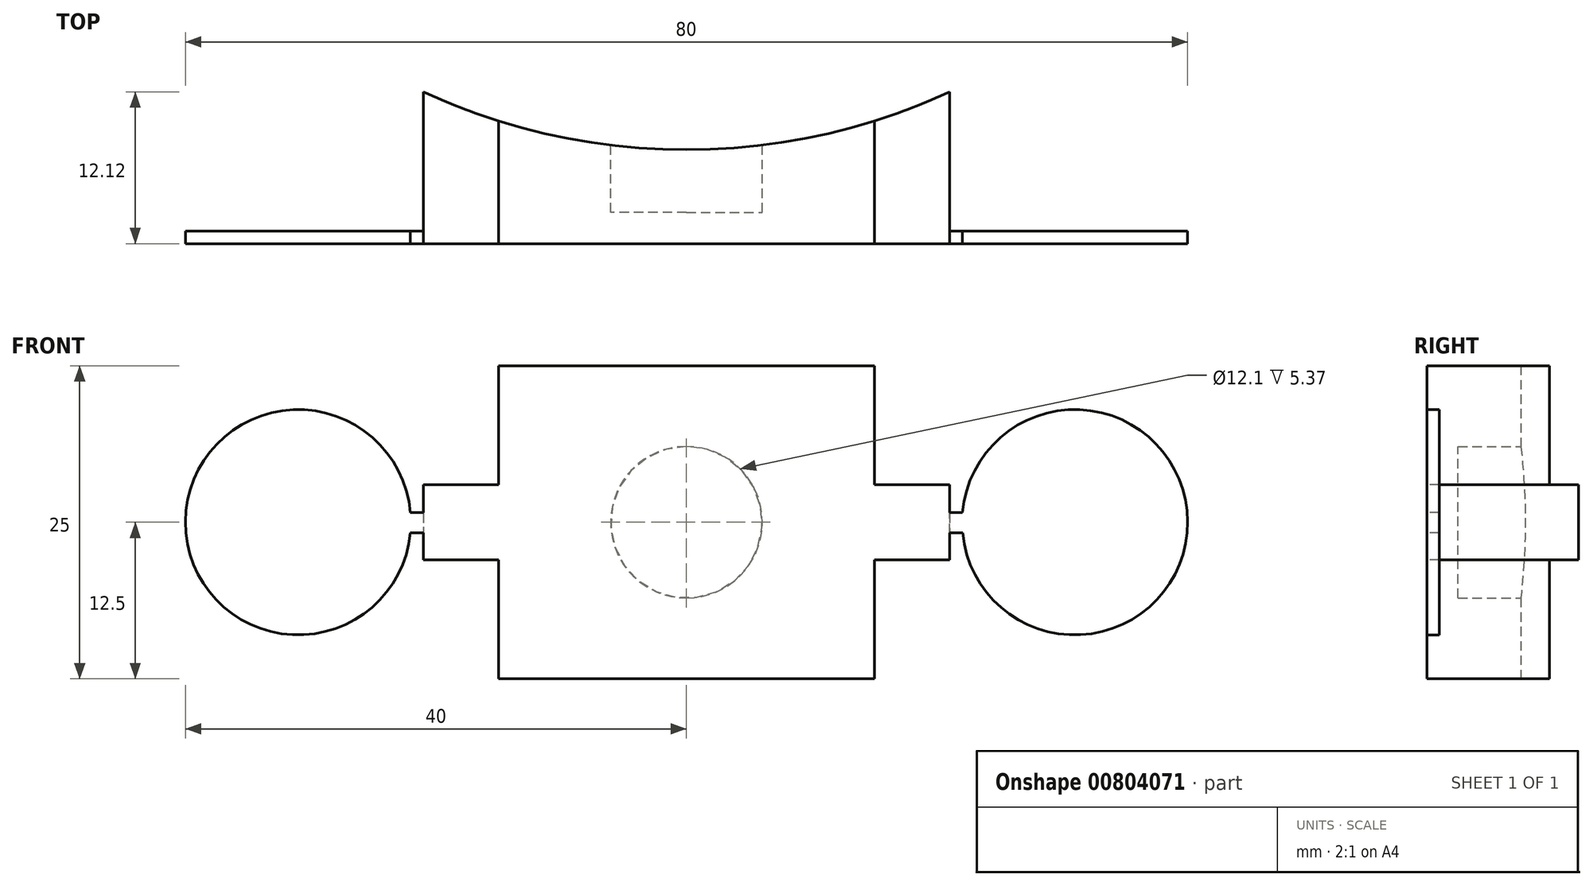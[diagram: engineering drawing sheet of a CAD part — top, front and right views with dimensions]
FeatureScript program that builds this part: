
annotation { "Feature Type Name" : "Feature", "Feature Type Description" : "" }
export const myFeature = defineFeature(function(context is Context, id is Id, definition is map)
    precondition{}
    {
        {
            var Q0;
            Q0=qCreatedBy(makeId("Top.planeOp"),FACE);
            var sketch = newSketch(context, id + "F0", { "sketchPlane" : qUnion([Q0])});
            skArc(sketch, "E0", {"start": v(-50, 0) * mm, "mid": v(0, -50) * mm, "end": v(50, 0) * mm});
            skArc(sketch, "E1", {"start": v(-55, 0) * mm, "mid": v(0, -55) * mm, "end": v(55, 0) * mm});
            skLineSegment(sketch, "E2", {"start": v(-55, 0) * mm, "end": v(-50, 0) * mm});
            skLineSegment(sketch, "E3.trimOffspring", {"start": v(50, 0) * mm, "end": v(55, 0) * mm});
            skSolve(sketch);
        }
        {
            var Q0;
            Q0=qSketchRegion(id+"F0",true);
            extrude(context, id + "F1", {"entities" : qUnion([Q0]), "endBound" : BoundingType.SYMMETRIC, "depth" : 25 * mm, "offsetDistance" : 25 * mm});
        }
        {
            var Q0;
            Q0=makeQuery(id+"F1.opExtrude","CAP_FACE",FACE,{"disambiguationData":[OSD([sQuery(id+"F0.wireOp",EDGE,"E0"),sQuery(id+"F0.wireOp",EDGE,"E1")])],"isStart":false});
            var sketch = newSketch(context, id + "F2", { "sketchPlane" : qUnion([Q0])});
            skLineSegment(sketch, "E4", {"start": v(-55, 0) * mm, "end": v(-55, -57.5) * mm});
            skLineSegment(sketch, "E5", {"start": v(55, 0) * mm, "end": v(55, -57.5) * mm});
            skLineSegment(sketch, "E6", {"start": v(0, -57.5) * mm, "end": v(55, -57.5) * mm});
            skLineSegment(sketch, "E7", {"start": v(0, -57.5) * mm, "end": v(-55, -57.5) * mm});
            skArc(sketch, "E8", {"start": v(-55, 0) * mm, "mid": v(0, -55) * mm, "end": v(55, 0) * mm});
            skLineSegment(sketch, "E9", {"start": v(0, -55) * mm, "end": v(0, -57.5) * mm, "construction": true});
            skSolve(sketch);
        }
        {
            var Q0;
            Q0=qSketchRegion(id+"F2",true);
            extrude(context, id + "F3", {"entities" : qUnion([Q0]), "operationType" : NewBodyOperationType.ADD, "oppositeDirection" : true, "depth" : 25 * mm, "offsetDistance" : 25 * mm});
        }
        {
            var Q0;
            Q0=qCreatedBy(makeId("Front.planeOp"),FACE);
            var sketch = newSketch(context, id + "F4", { "sketchPlane" : qUnion([Q0])});
            skCircle(sketch, "E10", {"center": v(0, 0) * mm, "radius": 6.05 * mm});
            skSolve(sketch);
        }
        {
            var Q0;
            Q0=qSketchRegion(id+"F4",true);
            extrude(context, id + "F5", {"entities" : qUnion([Q0]), "operationType" : NewBodyOperationType.REMOVE, "depth" : 55 * mm, "offsetDistance" : 25 * mm});
        }
        {
            var Q0;
            Q0=qCreatedBy(makeId("Right.planeOp"),FACE);
            var sketch = newSketch(context, id + "F6", { "sketchPlane" : qUnion([Q0])});
            skLineSegment(sketch, "E11", {"start": v(0, 0) * mm, "end": v(-11, 0) * mm, "construction": true});
            skCircle(sketch, "E12", {"center": v(-11, 0) * mm, "radius": 9.05 * mm});
            skSolve(sketch);
        }
        {
            var Q0;
            Q0=qSketchRegion(id+"F6",true);
            extrude(context, id + "F7", {"entities" : qUnion([Q0]), "operationType" : NewBodyOperationType.REMOVE, "endBound" : BoundingType.SYMMETRIC, "oppositeDirection" : true, "depth" : 105 * mm, "offsetDistance" : 25 * mm});
        }
        {
            var Q0;
            Q0=makeQuery(id+"F3.opExtrude","SWEPT_FACE",FACE,{"disambiguationData":[OSD([sQuery(id+"F2.wireOp",EDGE,"E6"),sQuery(id+"F2.wireOp",EDGE,"E7")])]});
            var sketch = newSketch(context, id + "F8", { "sketchPlane" : qUnion([Q0])});
            skLineSegment(sketch, "E13", {"start": v(55, 0) * mm, "end": v(65, 0) * mm, "construction": true});
            skLineSegment(sketch, "E14", {"start": v(-55, 0) * mm, "end": v(-65, 0) * mm, "construction": true});
            skArc(sketch, "E15", {"start": v(56.19, -1.83) * mm, "mid": v(74, 0.24) * mm, "end": v(56.1, 1.35) * mm});
            skArc(sketch, "E16", {"start": v(-56.02, 0.59) * mm, "mid": v(-74, -0.07) * mm, "end": v(-56.01, -0.44) * mm});
            skLineSegment(sketch, "E17", {"start": v(0, -12.5) * mm, "end": v(-55, -12.5) * mm, "construction": true});
            skLineSegment(sketch, "E18", {"start": v(-27.5, -12.5) * mm, "end": v(-27.5, -22.5) * mm, "construction": true});
            skLineSegment(sketch, "E19", {"start": v(0, -12.5) * mm, "end": v(55, -12.5) * mm, "construction": true});
            skLineSegment(sketch, "E20", {"start": v(27.5, -12.5) * mm, "end": v(27.5, -22.5) * mm, "construction": true});
            skLineSegment(sketch, "E21", {"start": v(-55, 12.5) * mm, "end": v(0, 12.5) * mm, "construction": true});
            skLineSegment(sketch, "E22", {"start": v(-27.5, 12.5) * mm, "end": v(-27.5, 22.5) * mm, "construction": true});
            skLineSegment(sketch, "E23", {"start": v(0, 12.5) * mm, "end": v(55, 12.5) * mm, "construction": true});
            skLineSegment(sketch, "E24", {"start": v(27.5, 12.5) * mm, "end": v(27.5, 22.5) * mm, "construction": true});
            skArc(sketch, "E25", {"start": v(26.67, -13.54) * mm, "mid": v(27.5, -31.5) * mm, "end": v(28.35, -13.54) * mm});
            skArc(sketch, "E26", {"start": v(-28.3, -13.54) * mm, "mid": v(-27.52, -31.5) * mm, "end": v(-26.66, -13.54) * mm});
            skArc(sketch, "E27", {"start": v(-26.33, 13.58) * mm, "mid": v(-27.67, 31.5) * mm, "end": v(-28.34, 13.54) * mm});
            skArc(sketch, "E28", {"start": v(28.64, 13.57) * mm, "mid": v(27.37, 31.5) * mm, "end": v(26.62, 13.54) * mm});
            skLineSegment(sketch, "E29", {"start": v(56.19, -1.83) * mm, "end": v(55, -1.83) * mm});
            skLineSegment(sketch, "E30", {"start": v(56.1, 1.35) * mm, "end": v(55, 1.35) * mm});
            skLineSegment(sketch, "E31", {"start": v(55, -1.83) * mm, "end": v(55, 1.35) * mm});
            skLineSegment(sketch, "E32", {"start": v(26.62, 13.54) * mm, "end": v(26.62, 12.5) * mm});
            skLineSegment(sketch, "E33", {"start": v(28.64, 13.57) * mm, "end": v(28.64, 12.5) * mm});
            skLineSegment(sketch, "E34", {"start": v(28.64, 12.5) * mm, "end": v(26.62, 12.5) * mm});
            skLineSegment(sketch, "E35", {"start": v(-28.34, 13.54) * mm, "end": v(-28.34, 12.5) * mm});
            skLineSegment(sketch, "E36", {"start": v(-26.33, 13.58) * mm, "end": v(-26.33, 12.5) * mm});
            skLineSegment(sketch, "E37", {"start": v(-26.33, 12.5) * mm, "end": v(-28.34, 12.5) * mm});
            skLineSegment(sketch, "E38", {"start": v(-56.02, 0.59) * mm, "end": v(-55, 0.59) * mm});
            skLineSegment(sketch, "E39", {"start": v(-56.01, -0.44) * mm, "end": v(-55, -0.44) * mm});
            skLineSegment(sketch, "E40", {"start": v(-55, -0.44) * mm, "end": v(-55, 0.59) * mm});
            skLineSegment(sketch, "E41", {"start": v(-28.3, -13.54) * mm, "end": v(-28.3, -12.5) * mm});
            skLineSegment(sketch, "E42", {"start": v(-26.66, -13.54) * mm, "end": v(-26.66, -12.5) * mm});
            skLineSegment(sketch, "E43", {"start": v(-26.66, -12.5) * mm, "end": v(-28.3, -12.5) * mm});
            skLineSegment(sketch, "E44", {"start": v(26.67, -13.54) * mm, "end": v(26.67, -12.5) * mm});
            skLineSegment(sketch, "E45", {"start": v(28.35, -13.54) * mm, "end": v(28.35, -12.5) * mm});
            skLineSegment(sketch, "E46", {"start": v(28.35, -12.5) * mm, "end": v(26.67, -12.5) * mm});
            skSolve(sketch);
        }
        {
            var Q0;
            Q0=qSketchRegion(id+"F8",true);
            extrude(context, id + "F9", {"entities" : qUnion([Q0]), "operationType" : NewBodyOperationType.ADD, "oppositeDirection" : true, "depth" : 3 * mm, "offsetDistance" : 25 * mm});
        }
        {
            var Q0;
            Q0=makeQuery(id+"F9.boolean.opBoolean","MERGE",FACE,{"derivedFrom":[makeQuery(id+"F3.opExtrude","SWEPT_FACE",FACE,{"disambiguationData":[OSD([sQuery(id+"F2.wireOp",EDGE,"E6"),sQuery(id+"F2.wireOp",EDGE,"E7")])]}),makeQuery(id+"F9.opExtrude","CAP_FACE",FACE,{"disambiguationData":[OSD([sQuery(id+"F8.wireOp",EDGE,"E15"),sQuery(id+"F8.wireOp",EDGE,"E29"),sQuery(id+"F8.wireOp",EDGE,"E30"),sQuery(id+"F8.wireOp",EDGE,"E31")])],"isStart":true}),makeQuery(id+"F9.opExtrude","CAP_FACE",FACE,{"disambiguationData":[OSD([sQuery(id+"F8.wireOp",EDGE,"E16"),sQuery(id+"F8.wireOp",EDGE,"E38"),sQuery(id+"F8.wireOp",EDGE,"E39"),sQuery(id+"F8.wireOp",EDGE,"E40")])],"isStart":true}),makeQuery(id+"F9.opExtrude","CAP_FACE",FACE,{"disambiguationData":[OSD([sQuery(id+"F8.wireOp",EDGE,"E25"),sQuery(id+"F8.wireOp",EDGE,"E44"),sQuery(id+"F8.wireOp",EDGE,"E45"),sQuery(id+"F8.wireOp",EDGE,"E46")])],"isStart":true}),makeQuery(id+"F9.opExtrude","CAP_FACE",FACE,{"disambiguationData":[OSD([sQuery(id+"F8.wireOp",EDGE,"E26"),sQuery(id+"F8.wireOp",EDGE,"E41"),sQuery(id+"F8.wireOp",EDGE,"E42"),sQuery(id+"F8.wireOp",EDGE,"E43")])],"isStart":true}),makeQuery(id+"F9.opExtrude","CAP_FACE",FACE,{"disambiguationData":[OSD([sQuery(id+"F8.wireOp",EDGE,"E27"),sQuery(id+"F8.wireOp",EDGE,"E35"),sQuery(id+"F8.wireOp",EDGE,"E36"),sQuery(id+"F8.wireOp",EDGE,"E37")])],"isStart":true}),makeQuery(id+"F9.opExtrude","CAP_FACE",FACE,{"disambiguationData":[OSD([sQuery(id+"F8.wireOp",EDGE,"E28"),sQuery(id+"F8.wireOp",EDGE,"E32"),sQuery(id+"F8.wireOp",EDGE,"E33"),sQuery(id+"F8.wireOp",EDGE,"E34")])],"isStart":true})]});
            var sketch = newSketch(context, id + "F10", { "sketchPlane" : qUnion([Q0])});
            skLineSegment(sketch, "E47", {"start": v(0, 12.5) * mm, "end": v(0, -12.5) * mm, "construction": true});
            skLineSegment(sketch, "E48.left", {"start": v(-15, 12.5) * mm, "end": v(-15, 3) * mm});
            skLineSegment(sketch, "E48.right", {"start": v(15, 12.5) * mm, "end": v(15, 3) * mm});
            skLineSegment(sketch, "E49", {"start": v(15, 0) * mm, "end": v(0, 0) * mm, "construction": true});
            skLineSegment(sketch, "E50", {"start": v(0, 0) * mm, "end": v(-15, 0) * mm, "construction": true});
            skLineSegment(sketch, "E51", {"start": v(-15, 0) * mm, "end": v(-21, 0) * mm, "construction": true});
            skLineSegment(sketch, "E52", {"start": v(-21, 0) * mm, "end": v(-21, 3) * mm});
            skLineSegment(sketch, "E53", {"start": v(-21, 3) * mm, "end": v(-15, 3) * mm});
            skLineSegment(sketch, "E54", {"start": v(-21, 0) * mm, "end": v(-21, -3) * mm});
            skLineSegment(sketch, "E55", {"start": v(-21, -3) * mm, "end": v(-15, -3) * mm});
            skLineSegment(sketch, "E56.trimOffspring", {"start": v(-15, -3) * mm, "end": v(-15, -12.5) * mm});
            skLineSegment(sketch, "E57", {"start": v(15, 0) * mm, "end": v(21, 0) * mm, "construction": true});
            skLineSegment(sketch, "E58", {"start": v(21, 0) * mm, "end": v(21, 3) * mm});
            skLineSegment(sketch, "E59", {"start": v(21, 3) * mm, "end": v(15, 3) * mm});
            skLineSegment(sketch, "E60", {"start": v(21, 0) * mm, "end": v(21, -3) * mm});
            skLineSegment(sketch, "E61", {"start": v(21, -3) * mm, "end": v(15, -3) * mm});
            skLineSegment(sketch, "E62.trimOffspring", {"start": v(15, -3) * mm, "end": v(15, -12.5) * mm});
            skLineSegment(sketch, "E63", {"start": v(15, 12.5) * mm, "end": v(15, 42.1) * mm});
            skLineSegment(sketch, "E64", {"start": v(15, 42.1) * mm, "end": v(79.78, 42.1) * mm});
            skLineSegment(sketch, "E65", {"start": v(79.78, 42.1) * mm, "end": v(79.78, -47.12) * mm});
            skLineSegment(sketch, "E66", {"start": v(79.78, -47.12) * mm, "end": v(15, -47.12) * mm});
            skLineSegment(sketch, "E67", {"start": v(15, -47.12) * mm, "end": v(15, -12.5) * mm});
            skLineSegment(sketch, "E68", {"start": v(-15, 12.5) * mm, "end": v(-15, 43.2) * mm});
            skLineSegment(sketch, "E69", {"start": v(-15, 43.2) * mm, "end": v(-80.15, 43.2) * mm});
            skLineSegment(sketch, "E70", {"start": v(-80.15, 43.2) * mm, "end": v(-80.15, -41.9) * mm});
            skLineSegment(sketch, "E71", {"start": v(-80.15, -41.9) * mm, "end": v(-15, -41.9) * mm});
            skLineSegment(sketch, "E72", {"start": v(-15, -41.9) * mm, "end": v(-15, -12.5) * mm});
            skSolve(sketch);
        }
        {
            var Q0;
            Q0=qSketchRegion(id+"F10",true);
            extrude(context, id + "F11", {"entities" : qUnion([Q0]), "operationType" : NewBodyOperationType.REMOVE, "endBound" : BoundingType.THROUGH_ALL, "oppositeDirection" : true, "depth" : 25 * mm, "offsetDistance" : 25 * mm});
        }
        {
            var Q0;
            Q0=makeQuery(id+"F9.boolean.opBoolean","MERGE",FACE,{"derivedFrom":[makeQuery(id+"F3.opExtrude","SWEPT_FACE",FACE,{"disambiguationData":[OSD([sQuery(id+"F2.wireOp",EDGE,"E6"),sQuery(id+"F2.wireOp",EDGE,"E7")])]}),makeQuery(id+"F9.opExtrude","CAP_FACE",FACE,{"disambiguationData":[OSD([sQuery(id+"F8.wireOp",EDGE,"E15"),sQuery(id+"F8.wireOp",EDGE,"E29"),sQuery(id+"F8.wireOp",EDGE,"E30"),sQuery(id+"F8.wireOp",EDGE,"E31")])],"isStart":true}),makeQuery(id+"F9.opExtrude","CAP_FACE",FACE,{"disambiguationData":[OSD([sQuery(id+"F8.wireOp",EDGE,"E16"),sQuery(id+"F8.wireOp",EDGE,"E38"),sQuery(id+"F8.wireOp",EDGE,"E39"),sQuery(id+"F8.wireOp",EDGE,"E40")])],"isStart":true}),makeQuery(id+"F9.opExtrude","CAP_FACE",FACE,{"disambiguationData":[OSD([sQuery(id+"F8.wireOp",EDGE,"E25"),sQuery(id+"F8.wireOp",EDGE,"E44"),sQuery(id+"F8.wireOp",EDGE,"E45"),sQuery(id+"F8.wireOp",EDGE,"E46")])],"isStart":true}),makeQuery(id+"F9.opExtrude","CAP_FACE",FACE,{"disambiguationData":[OSD([sQuery(id+"F8.wireOp",EDGE,"E26"),sQuery(id+"F8.wireOp",EDGE,"E41"),sQuery(id+"F8.wireOp",EDGE,"E42"),sQuery(id+"F8.wireOp",EDGE,"E43")])],"isStart":true}),makeQuery(id+"F9.opExtrude","CAP_FACE",FACE,{"disambiguationData":[OSD([sQuery(id+"F8.wireOp",EDGE,"E27"),sQuery(id+"F8.wireOp",EDGE,"E35"),sQuery(id+"F8.wireOp",EDGE,"E36"),sQuery(id+"F8.wireOp",EDGE,"E37")])],"isStart":true}),makeQuery(id+"F9.opExtrude","CAP_FACE",FACE,{"disambiguationData":[OSD([sQuery(id+"F8.wireOp",EDGE,"E28"),sQuery(id+"F8.wireOp",EDGE,"E32"),sQuery(id+"F8.wireOp",EDGE,"E33"),sQuery(id+"F8.wireOp",EDGE,"E34")])],"isStart":true})]});
            var sketch = newSketch(context, id + "F12", { "sketchPlane" : qUnion([Q0])});
            skLineSegment(sketch, "E73", {"start": v(21, 0) * mm, "end": v(31, 0) * mm, "construction": true});
            skLineSegment(sketch, "E74", {"start": v(-21, 0) * mm, "end": v(-31, 0) * mm, "construction": true});
            skArc(sketch, "E75", {"start": v(-22.03, 0.79) * mm, "mid": v(-40, 0.03) * mm, "end": v(-22.04, -0.85) * mm});
            skArc(sketch, "E76", {"start": v(22.04, -0.86) * mm, "mid": v(40, 0.04) * mm, "end": v(22.03, 0.78) * mm});
            skLineSegment(sketch, "E77", {"start": v(22.03, 0.78) * mm, "end": v(21, 0.78) * mm});
            skLineSegment(sketch, "E78", {"start": v(21, 0.78) * mm, "end": v(21, -0.86) * mm});
            skLineSegment(sketch, "E79", {"start": v(21, -0.86) * mm, "end": v(22.04, -0.86) * mm});
            skLineSegment(sketch, "E80", {"start": v(-22.04, -0.85) * mm, "end": v(-21, -0.85) * mm});
            skLineSegment(sketch, "E81", {"start": v(-21, -0.85) * mm, "end": v(-21, 0.79) * mm});
            skLineSegment(sketch, "E82", {"start": v(-21, 0.79) * mm, "end": v(-22.03, 0.79) * mm});
            skSolve(sketch);
        }
        {
            var Q0;
            Q0=qSketchRegion(id+"F12",true);
            extrude(context, id + "F13", {"entities" : qUnion([Q0]), "operationType" : NewBodyOperationType.ADD, "oppositeDirection" : true, "depth" : 1 * mm, "offsetDistance" : 25 * mm});
        }
    });
